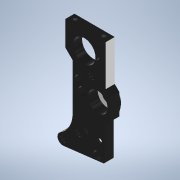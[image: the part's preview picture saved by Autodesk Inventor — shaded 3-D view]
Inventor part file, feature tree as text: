
AUTODESK INVENTOR PART (.ipt)
format: ipt  version: 2022 (Build 260153000, 153)  size: 642,560 bytes
history: native  units: mm
features: extrude x17, sketch x13, fillet x5, projected_geometry x5, thread x2, chamfer x2, other x2, mirror x1, reference x1
ambient origin geometry x8: Origin, YZ Plane, XZ Plane, XY Plane, X Axis, Y Axis, Z Axis, Center Point
bodies: Solid1 (feature_tree)
feature tree (48):
  extrude  "Extrusion1"  Depth=3.0mm
  fillet  "Fillet1"  Radius=23.5mm
  fillet  "Fillet2"  Radius=6.0mm
  extrude  "Extrusion2"  Depth=3.0mm
  extrude  "Extrusion3"  Depth=56.0mm
  thread  "Thread1"  [1 undecoded]
  thread  "Thread2"  [1 undecoded]
  extrude  "Extrusion4"  Depth=12.5mm
  extrude  "Extrusion5"  Depth=2.1mm
  extrude  "Extrusion6"  Depth=4.0mm
  extrude  "Extrusion7"  TaperAngle=45.0deg  [1 undecoded]
  extrude  "Extrusion8"  Depth=3.0mm
  extrude  "Extrusion9"  TaperAngle=135.0deg  [1 undecoded]
  extrude  "Extrusion10"  Depth=3.0mm TaperAngle=0.0deg
  fillet  "Fillet3"  Radius=3.0mm
  extrude  "Extrusion11"  Depth=3.0mm
  chamfer  "Chamfer1"  Distance=7.5mm
  fillet  "Fillet4"  Radius=2.5mm
  extrude  "Extrusion12"  Depth=10.0mm
  extrude  "Extrusion13"  Depth=10.0mm
  extrude  "Extrusion14"  Depth=1.0mm
  fillet  "Fillet5"  Radius=15.0mm
  mirror  "Mirror2"
  extrude  "Extrusion15"  Depth=10.0mm
  chamfer  "Chamfer2"  Distance=20.0mm
  extrude  "Extrusion16"  Depth=10.0mm
  extrude  "Extrusion17"  Depth=3.0mm TaperAngle=0.0deg
  sketch  "Sketch3"  dims[d0=3.0mm d1=6.0mm d2=23.5mm d3=6.0mm]
  projected_geometry  "Projected Loop1"
  sketch  "Sketch5"  dims[d4=0.0mm d5=3.0mm]
  sketch  "Sketch7"  dims[d6=18.0mm d7=56.0mm d8=11.0mm d9=4.0mm]
  sketch  "Sketch8"  dims[d10=24.75mm d11=12.5mm]
  projected_geometry  "Projected Loop2"
  sketch  "Sketch10"  dims[d12=22.3mm d14=2.1mm]
  sketch  "Sketch13"  dims[d18=30.0mm d20=360.0deg d22=4.0mm]
  sketch  "Sketch15"  dims[d23=14.0mm d24=45.0deg]
  sketch  "Sketch17"  dims[d25=3.0mm d26=12.0mm]
  projected_geometry  "Projected Loop3"
  sketch  "Sketch21"  dims[d27=6.0mm d28=135.0deg]
  projected_geometry  "Projected Loop5"
  sketch  "Sketch22"  dims[d29=135.0deg d30=5.0mm d31=0.0mm d32=3.0mm]
  projected_geometry  "Projected Loop6"
  sketch  "Sketch24"  dims[d33=10.0mm d34=3.0mm]
  sketch  "Sketch25"  dims[d35=2.5mm]
  sketch  "Sketch26"  dims[d36=13.5mm d37=7.5mm d38=2.5mm d39=15.0mm d40=12.5mm d41=1.0mm d42=15.0mm d43=12.75mm d44=20.0mm d45=23.75mm d46=3.0mm d47=0.0mm d48=2.0mm d49=2.0mm d50=2.5mm d51=2.5mm d52=3.0mm d53=3.0mm d54=4.5mm d55=0.0mm d56=7.0mm d57=0.0mm d58=7.0mm d59=0.0mm d60=8.5mm d61=270.0deg d62=4.0mm d63=4.0mm d64=4.0mm d65=3.0mm d66=0.0mm d67=5.5mm d68=2.0mm d69=0.0mm d70=4.0mm d71=1.85mm d72=4.0mm d73=1.85mm d74=1.0mm d75=2.8mm d76=2.8mm d77=1.0mm d78=10.0mm d79=0.0mm d82=3.1mm d83=11.15mm d84=2.1mm d85=2.1mm d86=2.1mm d87=5.5mm d88=3.5mm d89=25.75mm d90=30.25mm d91=2.5mm d92=11.75mm d93=24.0mm d94=8.0mm d95=2.1mm d96=2.1mm d98=2.1mm d99=1.8mm d100=0.0mm d101=2.1mm d102=2.1mm d103=2.1mm d104=1.8mm d105=0.0mm d117=3.9mm d118=0.0mm d119=18.0mm d120=6.5mm d121=0.0mm d122=1.0mm d125=5.0mm d126=7.25mm d127=2.5mm d128=5.0mm d129=15.0mm d130=5.0mm d131=5.0mm d132=90.0deg d133=135.0deg d135=135.0deg d136=135.0deg d137=3.0mm d138=0.0mm d139=0.9mm d140=2.0mm d141=45.0deg d142=4.0mm d143=2.0mm d144=2.6mm d145=3.625mm d146=10.0mm d147=0.0mm d148=2.05mm d149=2.4mm d150=0.0mm d151=4.5mm d154=1.0mm d155=0.0mm d156=2.0mm d157=2.8mm d158=1.0mm d159=1.5mm d160=0.0mm d161=1.5mm d162=2.0mm d163=45.0deg d164=6.0mm d165=0.5mm d166=10.0mm d167=0.0mm d168=0.5mm d169=0.0mm d80=0.5mm d81=0.872665mm d106=0.872665mm d123=0.872665mm d134=0.5mm d153=0.5mm]
  reference  "Reference1"
  other  "Dribbler-3-gears-new.iam"
  other  "Kugellager 685-ZZ-C3:2"
note: 4 required parameter values undecoded (feature->parameter linkage not recoverable at this tier; creation-order binding heuristic only, values carry confidence <= 0.55)
